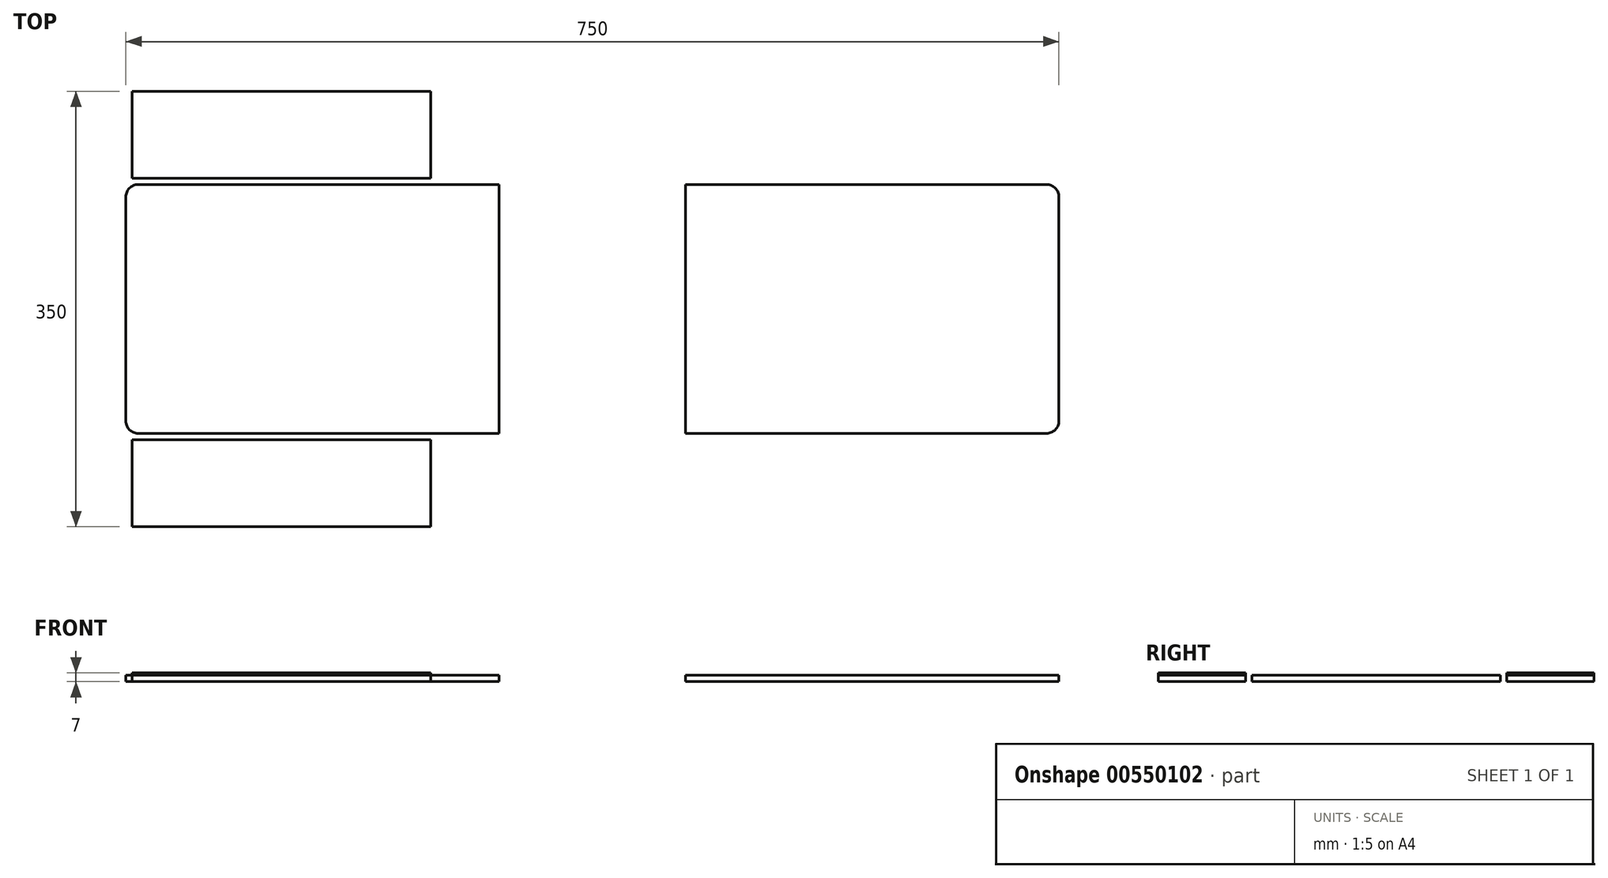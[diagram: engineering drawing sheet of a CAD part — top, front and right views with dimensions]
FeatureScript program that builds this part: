
annotation { "Feature Type Name" : "Feature", "Feature Type Description" : "" }
export const myFeature = defineFeature(function(context is Context, id is Id, definition is map)
    precondition{}
    {
        {
            var Q0;
            Q0=qCreatedBy(makeId("Top.planeOp"),FACE);
            var sketch = newSketch(context, id + "F0", { "sketchPlane" : qUnion([Q0])});
            skLineSegment(sketch, "E0.bottom", {"start": v(-450, -18.15) * mm, "end": v(300, -18.15) * mm});
            skLineSegment(sketch, "E0.top", {"start": v(-450, -218.15) * mm, "end": v(300, -218.15) * mm});
            skLineSegment(sketch, "E0.left", {"start": v(-450, -18.15) * mm, "end": v(-450, -218.15) * mm});
            skLineSegment(sketch, "E0.right", {"start": v(300, -18.15) * mm, "end": v(300, -218.15) * mm});
            skLineSegment(sketch, "E1.bottom", {"start": v(-450, -18.15) * mm, "end": v(-200, -18.15) * mm});
            skLineSegment(sketch, "E1.top", {"start": v(-450, 61.85) * mm, "end": v(-200, 61.85) * mm});
            skLineSegment(sketch, "E1.left", {"start": v(-450, -18.15) * mm, "end": v(-450, 61.85) * mm});
            skLineSegment(sketch, "E1.right", {"start": v(-200, -18.15) * mm, "end": v(-200, 61.85) * mm});
            skLineSegment(sketch, "E2.bottom", {"start": v(-450, -218.15) * mm, "end": v(-200, -218.15) * mm});
            skLineSegment(sketch, "E2.top", {"start": v(-450, -298.15) * mm, "end": v(-200, -298.15) * mm});
            skLineSegment(sketch, "E2.left", {"start": v(-450, -218.15) * mm, "end": v(-450, -298.15) * mm});
            skLineSegment(sketch, "E2.right", {"start": v(-200, -218.15) * mm, "end": v(-200, -298.15) * mm});
            skLineSegment(sketch, "E3.bottom", {"start": v(0, -218.15) * mm, "end": v(-150, -218.15) * mm});
            skLineSegment(sketch, "E3.top", {"start": v(0, -18.15) * mm, "end": v(-150, -18.15) * mm});
            skLineSegment(sketch, "E3.left", {"start": v(0, -218.15) * mm, "end": v(0, -18.15) * mm});
            skLineSegment(sketch, "E3.right", {"start": v(-150, -218.15) * mm, "end": v(-150, -18.15) * mm});
            skLineSegment(sketch, "E4.bottom", {"start": v(-445, 56.85) * mm, "end": v(-205, 56.85) * mm});
            skLineSegment(sketch, "E4.top", {"start": v(-445, -13.15) * mm, "end": v(-205, -13.15) * mm});
            skLineSegment(sketch, "E4.left", {"start": v(-445, 56.85) * mm, "end": v(-445, -13.15) * mm});
            skLineSegment(sketch, "E4.right", {"start": v(-205, 56.85) * mm, "end": v(-205, -13.15) * mm});
            skLineSegment(sketch, "E5.bottom", {"start": v(-445, -223.15) * mm, "end": v(-205, -223.15) * mm});
            skLineSegment(sketch, "E5.top", {"start": v(-445, -293.15) * mm, "end": v(-205, -293.15) * mm});
            skLineSegment(sketch, "E5.left", {"start": v(-445, -223.15) * mm, "end": v(-445, -293.15) * mm});
            skLineSegment(sketch, "E5.right", {"start": v(-205, -223.15) * mm, "end": v(-205, -293.15) * mm});
            skSolve(sketch);
        }
        {
            var Q0;
            Q0=makeQuery(id+"F0.imprint","IMPRINT",FACE,{"disambiguationData":[TD([[makeQuery(id+"F0.imprint","IMPRINT",EDGE,{"derivedFrom":sQuery(id+"F0.wireOp",EDGE,"E1.bottom")}),1.0]])]});
            var Q1;
            Q1=makeQuery(id+"F0.imprint","IMPRINT",FACE,{"disambiguationData":[TD([[makeQuery(id+"F0.imprint","IMPRINT",EDGE,{"derivedFrom":sQuery(id+"F0.wireOp",EDGE,"E4.bottom")}),-1.0]])]});
            var Q2;
            Q2=makeQuery(id+"F0.imprint","IMPRINT",FACE,{"disambiguationData":[TD([[makeQuery(id+"F0.imprint","IMPRINT",EDGE,{"derivedFrom":sQuery(id+"F0.wireOp",EDGE,"E0.left")}),1.0]])]});
            var Q3;
            Q3=makeQuery(id+"F0.imprint","IMPRINT",FACE,{"disambiguationData":[TD([[makeQuery(id+"F0.imprint","IMPRINT",EDGE,{"derivedFrom":sQuery(id+"F0.wireOp",EDGE,"E5.bottom")}),-1.0]])]});
            var Q4;
            Q4=makeQuery(id+"F0.imprint","IMPRINT",FACE,{"disambiguationData":[TD([[makeQuery(id+"F0.imprint","IMPRINT",EDGE,{"derivedFrom":sQuery(id+"F0.wireOp",EDGE,"E2.bottom")}),-1.0]])]});
            var Q5;
            Q5=makeQuery(id+"F0.imprint","IMPRINT",FACE,{"disambiguationData":[TD([[makeQuery(id+"F0.imprint","IMPRINT",EDGE,{"derivedFrom":sQuery(id+"F0.wireOp",EDGE,"E3.bottom")}),-1.0]])]});
            var Q6;
            {var subQ0=sQuery(id+"F0.wireOp",EDGE,"E0.right");Q6=makeQuery(id+"F0.imprint","IMPRINT",FACE,{"disambiguationData":[TD([[makeQuery(id+"F0.imprint","IMPRINT",EDGE,{"derivedFrom":subQ0}),-1.0]])]});}
            extrude(context, id + "F1", {"entities" : qUnion([Q0, Q1, Q2, Q3, Q4, Q5, Q6]), "depth" : 5 * mm, "offsetDistance" : 25 * mm});
        }
        {
            var Q0;
            Q0=makeQuery(id+"F0.imprint","IMPRINT",FACE,{"disambiguationData":[TD([[makeQuery(id+"F0.imprint","IMPRINT",EDGE,{"derivedFrom":sQuery(id+"F0.wireOp",EDGE,"E5.bottom")}),-1.0]])]});
            var Q1;
            Q1=makeQuery(id+"F0.imprint","IMPRINT",FACE,{"disambiguationData":[TD([[makeQuery(id+"F0.imprint","IMPRINT",EDGE,{"derivedFrom":sQuery(id+"F0.wireOp",EDGE,"E4.bottom")}),-1.0]])]});
            var Q2;
            Q2=makeQuery(id+"F0.imprint","IMPRINT",FACE,{"disambiguationData":[TD([[makeQuery(id+"F0.imprint","IMPRINT",EDGE,{"derivedFrom":sQuery(id+"F0.wireOp",EDGE,"E3.bottom")}),-1.0]])]});
            extrude(context, id + "F2", {"entities" : qUnion([Q0, Q1, Q2]), "depth" : 7 * mm, "offsetDistance" : 25 * mm});
        }
        {
            var Q0;
            Q0=makeQuery(id+"F1.opExtrude","SWEPT_EDGE",EDGE,{"disambiguationData":[OSD([sQuery(id+"F0.wireOp",EDGE,"E0.top"),sQuery(id+"F0.wireOp",EDGE,"E0.right")])]});
            var Q1;
            Q1=makeQuery(id+"F1.opExtrude","SWEPT_EDGE",EDGE,{"disambiguationData":[OSD([sQuery(id+"F0.wireOp",EDGE,"E0.bottom"),sQuery(id+"F0.wireOp",EDGE,"E0.right")])]});
            var Q2;
            Q2=makeQuery(id+"F1.opExtrude","SWEPT_EDGE",EDGE,{"disambiguationData":[OSD([sQuery(id+"F0.wireOp",EDGE,"E2.top"),sQuery(id+"F0.wireOp",EDGE,"E2.right")])]});
            var Q3;
            Q3=makeQuery(id+"F1.opExtrude","SWEPT_EDGE",EDGE,{"disambiguationData":[OSD([sQuery(id+"F0.wireOp",EDGE,"E2.top"),sQuery(id+"F0.wireOp",EDGE,"E2.left")])]});
            var Q4;
            Q4=makeQuery(id+"F1.opExtrude","SWEPT_EDGE",EDGE,{"disambiguationData":[OSD([sQuery(id+"F0.wireOp",EDGE,"E1.top"),sQuery(id+"F0.wireOp",EDGE,"E1.left")])]});
            var Q5;
            Q5=makeQuery(id+"F1.opExtrude","SWEPT_EDGE",EDGE,{"disambiguationData":[OSD([sQuery(id+"F0.wireOp",EDGE,"E1.top"),sQuery(id+"F0.wireOp",EDGE,"E1.right")])]});
            fillet(context, id + "F3", {"entities" : qUnion([Q0, Q1, Q2, Q3, Q4, Q5]), "radius" : 10 * mm, "tangentPropagation" : true, "allowEdgeOverflow" : false});
        }
    });
